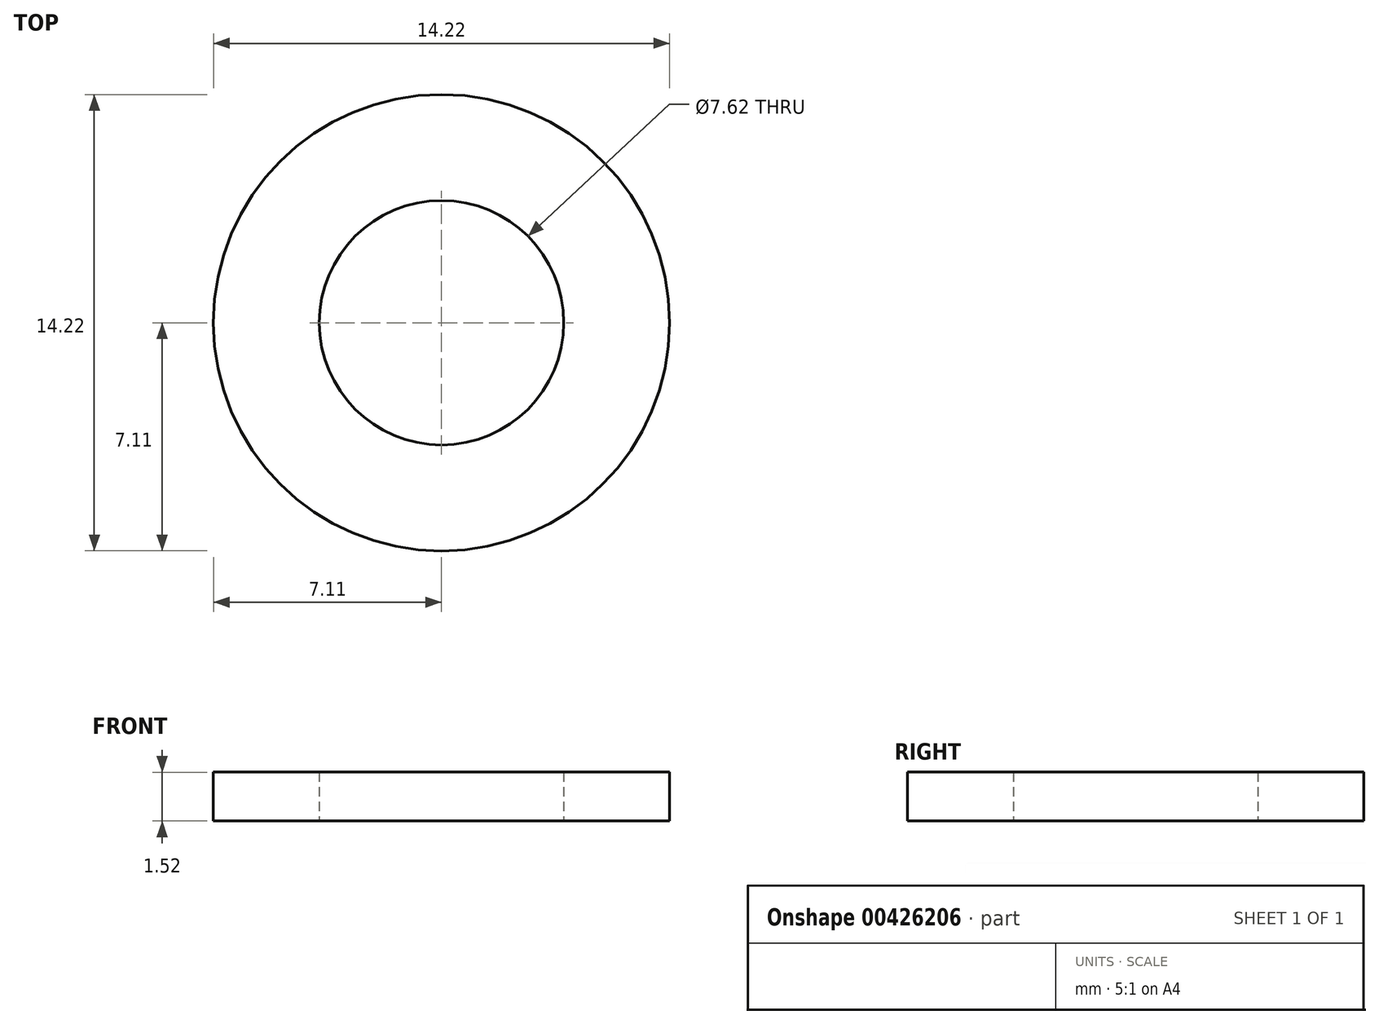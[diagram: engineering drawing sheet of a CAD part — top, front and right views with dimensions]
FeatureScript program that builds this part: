
annotation { "Feature Type Name" : "Feature", "Feature Type Description" : "" }
export const myFeature = defineFeature(function(context is Context, id is Id, definition is map)
    precondition{}
    {
        {
            var Q0;
            Q0=qCreatedBy(makeId("Top.planeOp"),FACE);
            var sketch = newSketch(context, id + "F0", { "sketchPlane" : qUnion([Q0])});
            skCircle(sketch, "E0", {"center": v(0, 0) * mm, "radius": 7.11 * mm});
            skCircle(sketch, "E1", {"center": v(0, 0) * mm, "radius": 3.81 * mm});
            skSolve(sketch);
        }
        {
            var Q0;
            Q0 = qSketchRegion(id + "F0", true);
            extrude(context, id + "F1", {"entities" : qUnion([Q0]), "depth" : 1.52 * mm});
        }
    });
